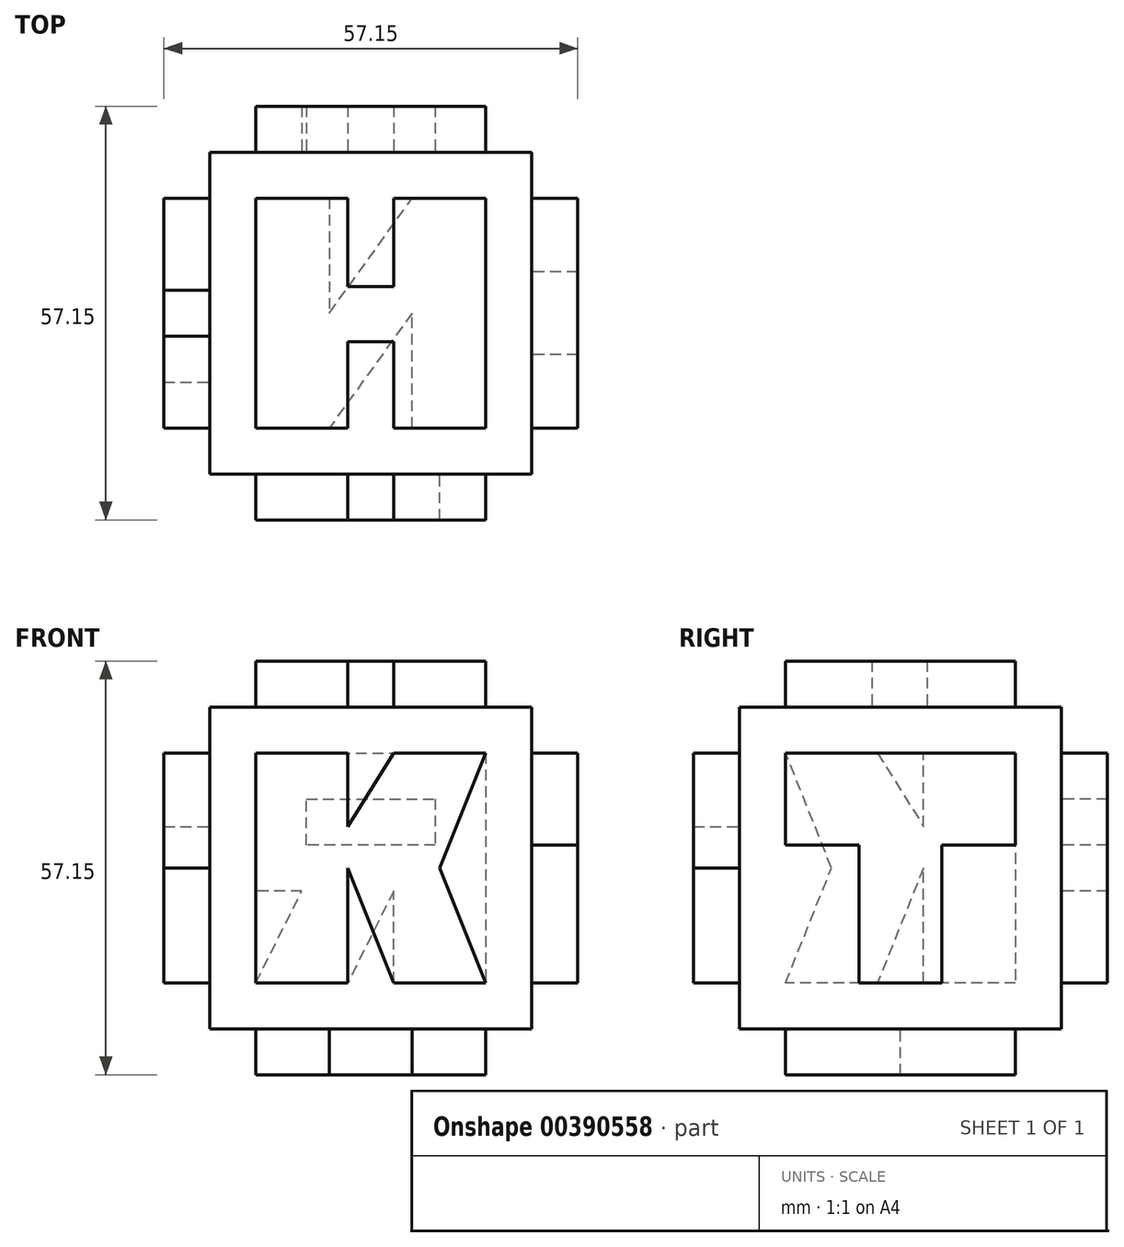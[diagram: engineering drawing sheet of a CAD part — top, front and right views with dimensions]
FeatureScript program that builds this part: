
annotation { "Feature Type Name" : "Feature", "Feature Type Description" : "" }
export const myFeature = defineFeature(function(context is Context, id is Id, definition is map)
    precondition{}
    {
        {
            var Q0;
            Q0=qCreatedBy(makeId("Front.planeOp"),FACE);
            var sketch = newSketch(context, id + "F0", { "sketchPlane" : qUnion([Q0])});
            skLineSegment(sketch, "E0", {"start": v(0, 0) * mm, "end": v(44.45, 0) * mm});
            skLineSegment(sketch, "E1", {"start": v(44.45, 0) * mm, "end": v(44.45, 44.45) * mm});
            skLineSegment(sketch, "E2", {"start": v(44.45, 44.45) * mm, "end": v(0, 44.45) * mm});
            skLineSegment(sketch, "E3", {"start": v(0, 44.45) * mm, "end": v(0, 0) * mm});
            skSolve(sketch);
        }
        {
            var Q0;
            Q0 = qSketchRegion(id + "F0", true);
            extrude(context, id + "F1", {"entities" : qUnion([Q0]), "depth" : 44.45 * mm});
        }
        {
            var Q0;
            Q0=makeQuery(id+"F1.opExtrude","CAP_FACE",FACE,{"disambiguationData":[OSD([sQuery(id+"F0.wireOp",EDGE,"E0"),sQuery(id+"F0.wireOp",EDGE,"E1"),sQuery(id+"F0.wireOp",EDGE,"E2"),sQuery(id+"F0.wireOp",EDGE,"E3")])],"isStart":false});
            var sketch = newSketch(context, id + "F2", { "sketchPlane" : qUnion([Q0])});
            skLineSegment(sketch, "E4", {"start": v(6.35, 38.1) * mm, "end": v(6.35, 6.35) * mm});
            skLineSegment(sketch, "E5", {"start": v(6.35, 6.35) * mm, "end": v(19.05, 6.35) * mm});
            skLineSegment(sketch, "E6", {"start": v(25.4, 6.35) * mm, "end": v(38.1, 6.35) * mm});
            skLineSegment(sketch, "E7", {"start": v(38.1, 6.35) * mm, "end": v(31.75, 22.23) * mm});
            skLineSegment(sketch, "E8", {"start": v(31.75, 22.23) * mm, "end": v(38.1, 38.1) * mm});
            skLineSegment(sketch, "E9", {"start": v(38.1, 38.1) * mm, "end": v(25.4, 38.1) * mm});
            skLineSegment(sketch, "E10", {"start": v(25.4, 6.35) * mm, "end": v(19.05, 22.23) * mm});
            skLineSegment(sketch, "E11", {"start": v(19.05, 22.23) * mm, "end": v(19.05, 6.35) * mm});
            skLineSegment(sketch, "E12", {"start": v(6.35, 38.1) * mm, "end": v(19.05, 38.1) * mm});
            skLineSegment(sketch, "E13", {"start": v(19.05, 38.1) * mm, "end": v(19.05, 27.94) * mm});
            skLineSegment(sketch, "E14", {"start": v(19.05, 27.94) * mm, "end": v(25.4, 38.1) * mm});
            skSolve(sketch);
        }
        {
            var Q0;
            Q0=makeQuery(id+"F1.opExtrude","SWEPT_FACE",FACE,{"disambiguationData":[OSD([sQuery(id+"F0.wireOp",EDGE,"E1")])]});
            var sketch = newSketch(context, id + "F3", { "sketchPlane" : qUnion([Q0])});
            skLineSegment(sketch, "E15", {"start": v(-27.94, 6.35) * mm, "end": v(-16.51, 6.35) * mm});
            skLineSegment(sketch, "E16", {"start": v(-16.51, 6.35) * mm, "end": v(-16.51, 25.4) * mm});
            skLineSegment(sketch, "E17", {"start": v(-16.51, 25.4) * mm, "end": v(-6.35, 25.4) * mm});
            skLineSegment(sketch, "E18", {"start": v(-6.35, 25.4) * mm, "end": v(-6.35, 38.1) * mm});
            skLineSegment(sketch, "E19", {"start": v(-6.35, 38.1) * mm, "end": v(-38.1, 38.1) * mm});
            skLineSegment(sketch, "E20", {"start": v(-38.1, 38.1) * mm, "end": v(-38.1, 25.4) * mm});
            skLineSegment(sketch, "E21", {"start": v(-38.1, 25.4) * mm, "end": v(-27.94, 25.4) * mm});
            skLineSegment(sketch, "E22", {"start": v(-27.94, 25.4) * mm, "end": v(-27.94, 6.35) * mm});
            skSolve(sketch);
        }
        {
            var Q0;
            Q0 = qSketchRegion(id + "F3", true);
            extrude(context, id + "F4", {"entities" : qUnion([Q0]), "operationType" : NewBodyOperationType.ADD, "depth" : 6.35 * mm});
        }
        {
            var Q0;
            Q0=qCreatedBy(makeId("Front.planeOp"),FACE);
            var sketch = newSketch(context, id + "F5", { "sketchPlane" : qUnion([Q0])});
            skLineSegment(sketch, "E23", {"start": v(38.1, 6.35) * mm, "end": v(25.4, 6.35) * mm});
            skLineSegment(sketch, "E24", {"start": v(25.4, 6.35) * mm, "end": v(25.4, 19.05) * mm});
            skLineSegment(sketch, "E25", {"start": v(25.4, 19.05) * mm, "end": v(19.05, 6.35) * mm});
            skLineSegment(sketch, "E26", {"start": v(19.05, 6.35) * mm, "end": v(6.35, 6.35) * mm});
            skLineSegment(sketch, "E27", {"start": v(6.35, 6.35) * mm, "end": v(12.7, 19.05) * mm});
            skLineSegment(sketch, "E28", {"start": v(12.7, 19.05) * mm, "end": v(6.35, 19.05) * mm});
            skLineSegment(sketch, "E29", {"start": v(6.35, 19.05) * mm, "end": v(6.35, 38.1) * mm});
            skLineSegment(sketch, "E30", {"start": v(6.35, 38.1) * mm, "end": v(38.1, 38.1) * mm});
            skLineSegment(sketch, "E31", {"start": v(38.1, 38.1) * mm, "end": v(38.1, 6.35) * mm});
            skLineSegment(sketch, "E32", {"start": v(31.12, 25.4) * mm, "end": v(13.34, 25.4) * mm});
            skLineSegment(sketch, "E33", {"start": v(13.34, 25.4) * mm, "end": v(13.34, 31.75) * mm});
            skLineSegment(sketch, "E34", {"start": v(13.34, 31.75) * mm, "end": v(31.12, 31.75) * mm});
            skLineSegment(sketch, "E35", {"start": v(31.12, 31.75) * mm, "end": v(31.12, 25.4) * mm});
            skSolve(sketch);
        }
        {
            var Q0;
            Q0 = qSketchRegion(id + "F5", true);
            extrude(context, id + "F6", {"entities" : qUnion([Q0]), "operationType" : NewBodyOperationType.ADD, "oppositeDirection" : true, "depth" : 6.35 * mm});
        }
        {
            var Q0;
            Q0=makeQuery(id+"F1.opExtrude","SWEPT_FACE",FACE,{"disambiguationData":[OSD([sQuery(id+"F0.wireOp",EDGE,"E2")])]});
            var sketch = newSketch(context, id + "F7", { "sketchPlane" : qUnion([Q0])});
            skLineSegment(sketch, "E36", {"start": v(6.35, -6.35) * mm, "end": v(6.35, -38.1) * mm});
            skLineSegment(sketch, "E37", {"start": v(6.35, -38.1) * mm, "end": v(19.05, -38.1) * mm});
            skLineSegment(sketch, "E38", {"start": v(19.05, -38.1) * mm, "end": v(19.05, -26.18) * mm});
            skLineSegment(sketch, "E39", {"start": v(19.05, -26.18) * mm, "end": v(25.4, -26.18) * mm});
            skLineSegment(sketch, "E40", {"start": v(25.4, -26.18) * mm, "end": v(25.4, -38.1) * mm});
            skLineSegment(sketch, "E41", {"start": v(25.4, -38.1) * mm, "end": v(38.1, -38.1) * mm});
            skLineSegment(sketch, "E42", {"start": v(38.1, -38.1) * mm, "end": v(38.1, -6.35) * mm});
            skLineSegment(sketch, "E43", {"start": v(38.1, -6.35) * mm, "end": v(25.4, -6.35) * mm});
            skLineSegment(sketch, "E44", {"start": v(25.4, -6.35) * mm, "end": v(25.4, -18.56) * mm});
            skLineSegment(sketch, "E45", {"start": v(25.4, -18.56) * mm, "end": v(19.05, -18.56) * mm});
            skLineSegment(sketch, "E46", {"start": v(19.05, -18.56) * mm, "end": v(19.05, -6.35) * mm});
            skLineSegment(sketch, "E47", {"start": v(19.05, -6.35) * mm, "end": v(6.35, -6.35) * mm});
            skSolve(sketch);
        }
        {
            var Q0;
            Q0 = qSketchRegion(id + "F7", true);
            extrude(context, id + "F8", {"entities" : qUnion([Q0]), "operationType" : NewBodyOperationType.ADD, "depth" : 6.35 * mm});
        }
        {
            var Q0;
            Q0=makeQuery(id+"F1.opExtrude","SWEPT_FACE",FACE,{"disambiguationData":[OSD([sQuery(id+"F0.wireOp",EDGE,"E0")])]});
            var sketch = newSketch(context, id + "F9", { "sketchPlane" : qUnion([Q0])});
            skLineSegment(sketch, "E48", {"start": v(6.35, 6.35) * mm, "end": v(16.51, 6.35) * mm});
            skLineSegment(sketch, "E49", {"start": v(16.51, 6.35) * mm, "end": v(16.51, 22.23) * mm});
            skLineSegment(sketch, "E50", {"start": v(16.51, 22.23) * mm, "end": v(27.94, 6.35) * mm});
            skLineSegment(sketch, "E51", {"start": v(27.94, 6.35) * mm, "end": v(38.1, 6.35) * mm});
            skLineSegment(sketch, "E52", {"start": v(38.1, 6.35) * mm, "end": v(38.1, 38.1) * mm});
            skLineSegment(sketch, "E53", {"start": v(38.1, 38.1) * mm, "end": v(27.94, 38.1) * mm});
            skLineSegment(sketch, "E54", {"start": v(27.94, 38.1) * mm, "end": v(27.94, 22.23) * mm});
            skLineSegment(sketch, "E55", {"start": v(27.94, 22.23) * mm, "end": v(16.51, 38.1) * mm});
            skLineSegment(sketch, "E56", {"start": v(16.51, 38.1) * mm, "end": v(6.35, 38.1) * mm});
            skLineSegment(sketch, "E57", {"start": v(6.35, 38.1) * mm, "end": v(6.35, 6.35) * mm});
            skSolve(sketch);
        }
        {
            var Q0;
            Q0 = qSketchRegion(id + "F9", true);
            extrude(context, id + "F10", {"entities" : qUnion([Q0]), "operationType" : NewBodyOperationType.ADD, "depth" : 6.35 * mm});
        }
        {
            var Q0;
            Q0 = qSketchRegion(id + "F2", true);
            extrude(context, id + "F11", {"entities" : qUnion([Q0]), "operationType" : NewBodyOperationType.ADD, "depth" : 6.35 * mm});
        }
        {
            var Q0;
            Q0=makeQuery(id+"F1.opExtrude","SWEPT_FACE",FACE,{"disambiguationData":[OSD([sQuery(id+"F0.wireOp",EDGE,"E3")])]});
            var sketch = newSketch(context, id + "F12", { "sketchPlane" : qUnion([Q0])});
            skLineSegment(sketch, "E58", {"start": v(6.35, 6.35) * mm, "end": v(19.05, 6.35) * mm});
            skLineSegment(sketch, "E59", {"start": v(19.05, 6.35) * mm, "end": v(19.05, 22.22) * mm});
            skLineSegment(sketch, "E60", {"start": v(19.05, 27.94) * mm, "end": v(19.05, 38.1) * mm});
            skLineSegment(sketch, "E61", {"start": v(19.05, 38.1) * mm, "end": v(6.35, 38.1) * mm});
            skLineSegment(sketch, "E62", {"start": v(6.35, 38.1) * mm, "end": v(6.35, 6.35) * mm});
            skLineSegment(sketch, "E63", {"start": v(19.05, 22.22) * mm, "end": v(25.4, 6.35) * mm});
            skLineSegment(sketch, "E64", {"start": v(25.4, 6.35) * mm, "end": v(38.1, 6.35) * mm});
            skLineSegment(sketch, "E65", {"start": v(38.1, 6.35) * mm, "end": v(31.75, 22.22) * mm});
            skLineSegment(sketch, "E66", {"start": v(31.75, 22.22) * mm, "end": v(38.1, 38.1) * mm});
            skLineSegment(sketch, "E67", {"start": v(38.1, 38.1) * mm, "end": v(25.4, 38.1) * mm});
            skLineSegment(sketch, "E68", {"start": v(25.4, 38.1) * mm, "end": v(19.05, 27.94) * mm});
            skSolve(sketch);
        }
        {
            var Q0;
            Q0 = qSketchRegion(id + "F12", true);
            extrude(context, id + "F13", {"entities" : qUnion([Q0]), "operationType" : NewBodyOperationType.ADD, "depth" : 6.35 * mm});
        }
        {
            var Q0;
            Q0 = qSketchRegion(id + "F5", true);
            var Q1;
            Q1=makeQuery(id+"F6.boolean.opBoolean","SPLIT",FACE,{"disambiguationData":[TD([makeQuery(id+"F6.opExtrude","SWEPT_FACE",FACE,{"disambiguationData":[OSD([sQuery(id+"F5.wireOp",EDGE,"E32")])]})])],"derivedFrom":makeQuery(id+"F1.opExtrude","CAP_FACE",FACE,{"disambiguationData":[OSD([sQuery(id+"F0.wireOp",EDGE,"E0"),sQuery(id+"F0.wireOp",EDGE,"E1"),sQuery(id+"F0.wireOp",EDGE,"E2"),sQuery(id+"F0.wireOp",EDGE,"E3")])],"isStart":true})});
            extrude(context, id + "F14", {"entities" : qUnion([Q0, Q1]), "operationType" : NewBodyOperationType.ADD, "depth" : 6.35 * mm});
        }
    });
